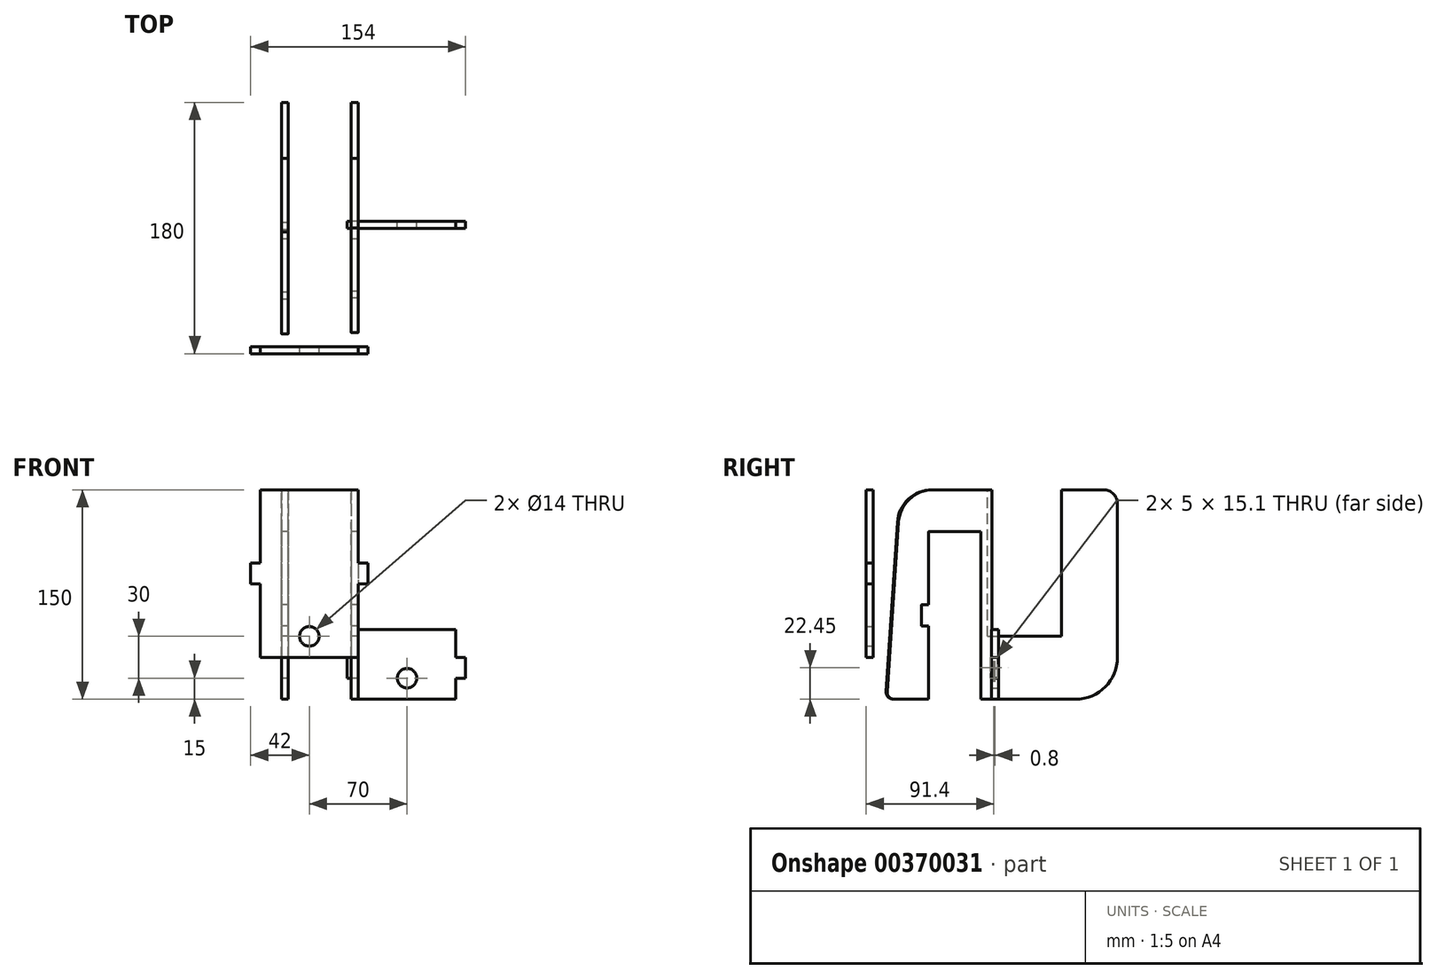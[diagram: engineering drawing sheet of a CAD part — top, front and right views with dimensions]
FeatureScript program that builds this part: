
annotation { "Feature Type Name" : "Feature", "Feature Type Description" : "" }
export const myFeature = defineFeature(function(context is Context, id is Id, definition is map)
    precondition{}
    {
        {
            var Q0;
            Q0=qCreatedBy(makeId("Right.planeOp"),FACE);
            var sketch = newSketch(context, id + "F0", { "sketchPlane" : qUnion([Q0])});
            skLineSegment(sketch, "E0.bottom", {"start": v(0, 0) * mm, "end": v(60, 0) * mm, "construction": true});
            skLineSegment(sketch, "E0.top", {"start": v(0, -105) * mm, "end": v(60, -105) * mm, "construction": true});
            skLineSegment(sketch, "E0.left", {"start": v(0, 0) * mm, "end": v(0, -105) * mm, "construction": true});
            skLineSegment(sketch, "E0.right", {"start": v(60, 0) * mm, "end": v(60, -105) * mm, "construction": true});
            skLineSegment(sketch, "E1", {"start": v(5, 0) * mm, "end": v(5, -105) * mm});
            skLineSegment(sketch, "E2", {"start": v(5, -105) * mm, "end": v(55, -105) * mm});
            skLineSegment(sketch, "E3", {"start": v(55, -105) * mm, "end": v(55, 0) * mm});
            skLineSegment(sketch, "E4", {"start": v(55, 0) * mm, "end": v(85, 0) * mm});
            skLineSegment(sketch, "E5", {"start": v(95, -10) * mm, "end": v(95, -120) * mm});
            skLineSegment(sketch, "E6", {"start": v(65, -150) * mm, "end": v(4.7, -150) * mm});
            skLineSegment(sketch, "E7", {"start": v(4.7, -150) * mm, "end": v(4.7, -97.55) * mm, "construction": true});
            skLineSegment(sketch, "E8", {"start": v(4.7, -30) * mm, "end": v(-40.3, -30) * mm});
            skLineSegment(sketch, "E9", {"start": v(-40.3, -30) * mm, "end": v(-40.3, -82.45) * mm});
            skLineSegment(sketch, "E10", {"start": v(-40.3, -150) * mm, "end": v(-64.96, -150) * mm});
            skLineSegment(sketch, "E11", {"start": v(-69.94, -144.67) * mm, "end": v(-61.86, -23.34) * mm});
            skLineSegment(sketch, "E12", {"start": v(-36.91, 0) * mm, "end": v(0, 0) * mm});
            skLineSegment(sketch, "E13.bottom", {"start": v(-40.3, -82.45) * mm, "end": v(-45.3, -82.45) * mm});
            skLineSegment(sketch, "E13.top", {"start": v(-40.3, -97.55) * mm, "end": v(-45.3, -97.55) * mm});
            skLineSegment(sketch, "E13.right", {"start": v(-45.3, -82.45) * mm, "end": v(-45.3, -97.55) * mm});
            skLineSegment(sketch, "E14.bottom", {"start": v(4.7, -82.45) * mm, "end": v(9.7, -82.45) * mm});
            skLineSegment(sketch, "E14.top", {"start": v(4.7, -97.55) * mm, "end": v(9.7, -97.55) * mm});
            skLineSegment(sketch, "E14.right", {"start": v(9.7, -82.45) * mm, "end": v(9.7, -97.55) * mm, "construction": true});
            skPoint(sketch, "E15", {"position": v(-40.3, -90) * mm});
            skLineSegment(sketch, "E16.trimOffspring", {"start": v(-40.3, -97.55) * mm, "end": v(-40.3, -150) * mm});
            skLineSegment(sketch, "E17.trimOffspring", {"start": v(4.7, -82.45) * mm, "end": v(4.7, -30) * mm, "construction": true});
            skLineSegment(sketch, "E18", {"start": v(-36.91, 0) * mm, "end": v(5, 0) * mm});
            skPoint(sketch, "E19.visualSharp", {"position": v(95, -150) * mm});
            skArc(sketch, "E19.filletArc", {"start": v(65, -150) * mm, "mid": v(86.21, -141.21) * mm, "end": v(95, -120) * mm});
            skPoint(sketch, "E20.visualSharp", {"position": v(95, 0) * mm});
            skArc(sketch, "E20.filletArc", {"start": v(95, -10) * mm, "mid": v(92.07, -2.93) * mm, "end": v(85, 0) * mm});
            skPoint(sketch, "E21.visualSharp", {"position": v(-60.3, 0) * mm});
            skArc(sketch, "E21.filletArc", {"start": v(-36.91, 0) * mm, "mid": v(-54, -6.74) * mm, "end": v(-61.86, -23.34) * mm});
            skPoint(sketch, "E22.visualSharp", {"position": v(-70.3, -150) * mm});
            skArc(sketch, "E22.filletArc", {"start": v(-69.94, -144.67) * mm, "mid": v(-68.6, -148.42) * mm, "end": v(-64.96, -150) * mm});
            skPoint(sketch, "E23", {"position": v(-17.8, -30) * mm});
            skPoint(sketch, "E24", {"position": v(-169.24, -72.15) * mm});
            skLineSegment(sketch, "E25", {"start": v(-7.8, -30) * mm, "end": v(-7.8, -150) * mm, "construction": true});
            skLineSegment(sketch, "E26", {"start": v(-2.8, -30) * mm, "end": v(-2.8, -150) * mm});
            skLineSegment(sketch, "E27", {"start": v(-2.8, -150) * mm, "end": v(4.7, -150) * mm});
            skLineSegment(sketch, "E28", {"start": v(4.7, -82.45) * mm, "end": v(4.7, -97.55) * mm});
            skPoint(sketch, "E29", {"position": v(4.7, -120) * mm});
            skLineSegment(sketch, "E30.bottom", {"start": v(4.7, -120) * mm, "end": v(9.7, -120) * mm});
            skLineSegment(sketch, "E30.top", {"start": v(4.7, -135.1) * mm, "end": v(9.7, -135.1) * mm});
            skLineSegment(sketch, "E30.left", {"start": v(4.7, -120) * mm, "end": v(4.7, -135.1) * mm});
            skLineSegment(sketch, "E30.right", {"start": v(9.7, -120) * mm, "end": v(9.7, -135.1) * mm});
            skSolve(sketch);
        }
        {
            var Q0;
            Q0=qSketchRegion(id+"F0",true);
            extrude(context, id + "F1", {"entities" : qUnion([Q0]), "depth" : 5 * mm});
        }
        {
            var Q0;
            Q0=makeQuery(id+"F1.opExtrude","SWEPT_FACE",FACE,{"disambiguationData":[OSD([sQuery(id+"F0.wireOp",EDGE,"E30.right")])]});
            var sketch = newSketch(context, id + "F2", { "sketchPlane" : qUnion([Q0])});
            skLineSegment(sketch, "E31.bottom", {"start": v(5, -30) * mm, "end": v(75, -30) * mm});
            skLineSegment(sketch, "E31.top", {"start": v(5, -150) * mm, "end": v(75, -150) * mm});
            skLineSegment(sketch, "E31.left", {"start": v(5, -30) * mm, "end": v(5, -150) * mm});
            skLineSegment(sketch, "E31.right", {"start": v(75, -30) * mm, "end": v(75, -150) * mm});
            skLineSegment(sketch, "E32.bottom", {"start": v(5, -120) * mm, "end": v(-3, -120) * mm});
            skLineSegment(sketch, "E32.top", {"start": v(5, -135) * mm, "end": v(-3, -135) * mm});
            skLineSegment(sketch, "E32.left", {"start": v(5, -120) * mm, "end": v(5, -135) * mm});
            skLineSegment(sketch, "E32.right", {"start": v(-3, -120) * mm, "end": v(-3, -135) * mm});
            skLineSegment(sketch, "E33.bottom", {"start": v(75, -120) * mm, "end": v(82, -120) * mm});
            skLineSegment(sketch, "E33.top", {"start": v(75, -135) * mm, "end": v(82, -135) * mm});
            skLineSegment(sketch, "E33.left", {"start": v(75, -120) * mm, "end": v(75, -135) * mm});
            skLineSegment(sketch, "E33.right", {"start": v(82, -120) * mm, "end": v(82, -135) * mm});
            skCircle(sketch, "E34", {"center": v(40, -135) * mm, "radius": 7 * mm});
            skPoint(sketch, "E35", {"position": v(40, -30) * mm});
            skPoint(sketch, "E36", {"position": v(75, -90) * mm});
            skPoint(sketch, "E37", {"position": v(75, -100) * mm});
            skLineSegment(sketch, "E38", {"start": v(75, -100) * mm, "end": v(5, -100) * mm});
            skSolve(sketch);
        }
        {
            var Q0;
            Q0=makeQuery(id+"F2.imprint","IMPRINT",FACE,{"disambiguationData":[TD([[makeQuery(id+"F2.imprint","IMPRINT",EDGE,{"derivedFrom":sQuery(id+"F2.wireOp",EDGE,"E33.bottom")}),-1.0]])]});
            var Q1;
            {var subQ2=sQuery(id+"F2.wireOp",EDGE,"E31.top");Q1=makeQuery(id+"F2.imprint","IMPRINT",FACE,{"disambiguationData":[TD([[makeQuery(id+"F2.imprint","IMPRINT",EDGE,{"derivedFrom":subQ2}),1.0]])]});}
            var Q2;
            {var subQ3=sQuery(id+"F2.wireOp",EDGE,"E32.right");Q2=makeQuery(id+"F2.imprint","IMPRINT",FACE,{"disambiguationData":[TD([[makeQuery(id+"F2.imprint","IMPRINT",EDGE,{"derivedFrom":subQ3}),1.0]])]});}
            var Q3;
            {var subQ3=sQuery(id+"F2.wireOp",EDGE,"E32.left");Q3=makeQuery(id+"F2.imprint","IMPRINT",FACE,{"disambiguationData":[TD([[makeQuery(id+"F2.imprint","IMPRINT",EDGE,{"derivedFrom":subQ3}),-1.0]])]});}
            extrude(context, id + "F3", {"entities" : qUnion([Q0, Q1, Q2, Q3]), "depth" : 5 * mm});
        }
        {
            var Q0;
            Q0=qCreatedBy(makeId("Right.planeOp"),FACE);
            cPlane(context, id + "F4", {"entities" : qUnion([Q0]), "cplaneType" : CPlaneType.OFFSET, "offset" : 50 * mm, "oppositeDirection" : true, "width" : 150 * mm, "height" : 150 * mm});
        }
        {
            var Q0;
            Q0=qCreatedBy(id+"F4.planeOp",FACE);
            var sketch = newSketch(context, id + "F5", { "sketchPlane" : qUnion([Q0])});
            skLineSegment(sketch, "E39.bottom", {"start": v(0, 0) * mm, "end": v(60, 0) * mm, "construction": true});
            skLineSegment(sketch, "E39.top", {"start": v(0, -105) * mm, "end": v(60, -105) * mm, "construction": true});
            skLineSegment(sketch, "E39.left", {"start": v(0, 0) * mm, "end": v(0, -105) * mm, "construction": true});
            skLineSegment(sketch, "E39.right", {"start": v(60, 0) * mm, "end": v(60, -105) * mm, "construction": true});
            skLineSegment(sketch, "E40", {"start": v(5, 0) * mm, "end": v(5, -105) * mm});
            skLineSegment(sketch, "E41", {"start": v(5, -105) * mm, "end": v(55, -105) * mm});
            skLineSegment(sketch, "E42", {"start": v(55, -105) * mm, "end": v(55, 0) * mm});
            skLineSegment(sketch, "E43", {"start": v(55, 0) * mm, "end": v(85, 0) * mm});
            skLineSegment(sketch, "E44", {"start": v(95, -10) * mm, "end": v(95, -120) * mm});
            skLineSegment(sketch, "E45", {"start": v(65, -150) * mm, "end": v(3.9, -150) * mm});
            skLineSegment(sketch, "E46", {"start": v(3.9, -150) * mm, "end": v(3.9, -97.55) * mm, "construction": true});
            skLineSegment(sketch, "E47", {"start": v(3.9, -30) * mm, "end": v(-41.1, -30) * mm});
            skLineSegment(sketch, "E48", {"start": v(-41.1, -30) * mm, "end": v(-41.1, -82.45) * mm});
            skLineSegment(sketch, "E49", {"start": v(-41.1, -150) * mm, "end": v(-65.76, -150) * mm});
            skLineSegment(sketch, "E50", {"start": v(-70.74, -144.67) * mm, "end": v(-62.66, -23.34) * mm});
            skLineSegment(sketch, "E51", {"start": v(-37.71, 0) * mm, "end": v(0, 0) * mm});
            skLineSegment(sketch, "E52.bottom", {"start": v(-41.1, -82.45) * mm, "end": v(-46.1, -82.45) * mm});
            skLineSegment(sketch, "E52.top", {"start": v(-41.1, -97.55) * mm, "end": v(-46.1, -97.55) * mm});
            skLineSegment(sketch, "E52.right", {"start": v(-46.1, -82.45) * mm, "end": v(-46.1, -97.55) * mm});
            skLineSegment(sketch, "E53.bottom", {"start": v(3.9, -82.45) * mm, "end": v(8.9, -82.45) * mm});
            skLineSegment(sketch, "E53.top", {"start": v(3.9, -97.55) * mm, "end": v(8.9, -97.55) * mm});
            skLineSegment(sketch, "E53.right", {"start": v(8.9, -82.45) * mm, "end": v(8.9, -97.55) * mm, "construction": true});
            skPoint(sketch, "E54", {"position": v(-41.1, -90) * mm});
            skLineSegment(sketch, "E55.trimOffspring", {"start": v(-41.1, -97.55) * mm, "end": v(-41.1, -150) * mm});
            skLineSegment(sketch, "E56.trimOffspring", {"start": v(3.9, -82.45) * mm, "end": v(3.9, -30) * mm, "construction": true});
            skLineSegment(sketch, "E57", {"start": v(-37.71, 0) * mm, "end": v(5, 0) * mm});
            skPoint(sketch, "E58.visualSharp", {"position": v(95, -150) * mm});
            skArc(sketch, "E58.filletArc", {"start": v(65, -150) * mm, "mid": v(86.21, -141.21) * mm, "end": v(95, -120) * mm});
            skPoint(sketch, "E59.visualSharp", {"position": v(95, 0) * mm});
            skArc(sketch, "E59.filletArc", {"start": v(95, -10) * mm, "mid": v(92.07, -2.93) * mm, "end": v(85, 0) * mm});
            skPoint(sketch, "E60.visualSharp", {"position": v(-61.1, 0) * mm});
            skArc(sketch, "E60.filletArc", {"start": v(-37.71, 0) * mm, "mid": v(-54.8, -6.74) * mm, "end": v(-62.66, -23.34) * mm});
            skPoint(sketch, "E61.visualSharp", {"position": v(-71.1, -150) * mm});
            skArc(sketch, "E61.filletArc", {"start": v(-70.74, -144.67) * mm, "mid": v(-69.4, -148.42) * mm, "end": v(-65.76, -150) * mm});
            skPoint(sketch, "E62", {"position": v(-18.6, -30) * mm});
            skPoint(sketch, "E63", {"position": v(-167.86, 8.95) * mm});
            skLineSegment(sketch, "E64", {"start": v(-8.6, -30) * mm, "end": v(-8.6, -150) * mm, "construction": true});
            skLineSegment(sketch, "E65", {"start": v(-2.8, -30) * mm, "end": v(-2.8, -150) * mm});
            skLineSegment(sketch, "E66", {"start": v(-2.8, -150) * mm, "end": v(3.9, -150) * mm});
            skLineSegment(sketch, "E67", {"start": v(3.9, -82.45) * mm, "end": v(3.9, -97.55) * mm});
            skPoint(sketch, "E68", {"position": v(3.9, -120) * mm});
            skLineSegment(sketch, "E69.bottom", {"start": v(3.9, -120) * mm, "end": v(8.9, -120) * mm});
            skLineSegment(sketch, "E69.top", {"start": v(3.9, -135.1) * mm, "end": v(8.9, -135.1) * mm});
            skLineSegment(sketch, "E69.left", {"start": v(3.9, -120) * mm, "end": v(3.9, -135.1) * mm});
            skLineSegment(sketch, "E69.right", {"start": v(8.9, -120) * mm, "end": v(8.9, -135.1) * mm});
            skLineSegment(sketch, "E70", {"start": v(5, -105) * mm, "end": v(2, -105) * mm});
            skLineSegment(sketch, "E71", {"start": v(2, -105) * mm, "end": v(2, 0) * mm});
            skSolve(sketch);
        }
        {
            var Q0;
            {var subQ7=sQuery(id+"F5.wireOp",EDGE,"E48");Q0=makeQuery(id+"F5.imprint","IMPRINT",FACE,{"disambiguationData":[TD([[makeQuery(id+"F5.imprint","IMPRINT",EDGE,{"derivedFrom":subQ7}),-1.0]])]});}
            var Q1;
            Q1=makeQuery(id+"F5.imprint","IMPRINT",FACE,{"disambiguationData":[TD([[makeQuery(id+"F5.imprint","IMPRINT",EDGE,{"derivedFrom":sQuery(id+"F5.wireOp",EDGE,"E41")}),-1.0]])]});
            extrude(context, id + "F6", {"entities" : qUnion([Q0, Q1]), "depth" : 5 * mm});
        }
        {
            var Q0;
            Q0=qCreatedBy(makeId("Front.planeOp"),FACE);
            cPlane(context, id + "F7", {"entities" : qUnion([Q0]), "cplaneType" : CPlaneType.OFFSET, "offset" : 80 * mm, "width" : 150 * mm, "height" : 150 * mm});
        }
        {
            var Q0;
            Q0=qCreatedBy(id+"F7.planeOp",FACE);
            var sketch = newSketch(context, id + "F8", { "sketchPlane" : qUnion([Q0])});
            skLineSegment(sketch, "E72.bottom", {"start": v(-65, 0) * mm, "end": v(5, 0) * mm});
            skLineSegment(sketch, "E72.top", {"start": v(-65, -120) * mm, "end": v(5, -120) * mm});
            skLineSegment(sketch, "E72.left", {"start": v(-65, 0) * mm, "end": v(-65, -120) * mm});
            skLineSegment(sketch, "E72.right", {"start": v(5, 0) * mm, "end": v(5, -120) * mm});
            skLineSegment(sketch, "E73.bottom", {"start": v(-65, -52.55) * mm, "end": v(-72, -52.55) * mm});
            skLineSegment(sketch, "E73.top", {"start": v(-65, -67.55) * mm, "end": v(-72, -67.55) * mm});
            skLineSegment(sketch, "E73.left", {"start": v(-65, -52.55) * mm, "end": v(-65, -67.55) * mm});
            skLineSegment(sketch, "E73.right", {"start": v(-72, -52.55) * mm, "end": v(-72, -67.55) * mm});
            skLineSegment(sketch, "E74.bottom", {"start": v(5, -52.55) * mm, "end": v(12, -52.55) * mm});
            skLineSegment(sketch, "E74.top", {"start": v(5, -67.55) * mm, "end": v(12, -67.55) * mm});
            skLineSegment(sketch, "E74.left", {"start": v(5, -52.55) * mm, "end": v(5, -67.55) * mm});
            skLineSegment(sketch, "E74.right", {"start": v(12, -52.55) * mm, "end": v(12, -67.55) * mm});
            skCircle(sketch, "E75", {"center": v(-30, -105) * mm, "radius": 7 * mm});
            skPoint(sketch, "E76", {"position": v(-30, 0) * mm});
            skPoint(sketch, "E77", {"position": v(5, -60) * mm});
            skPoint(sketch, "E78", {"position": v(5, -70) * mm});
            skLineSegment(sketch, "E79", {"start": v(5, -70) * mm, "end": v(-65, -70) * mm});
            skSolve(sketch);
        }
        {
            var Q0;
            Q0 = qSketchRegion(id + "F8", true);
            extrude(context, id + "F9", {"entities" : qUnion([Q0]), "depth" : 5 * mm});
        }
    });
